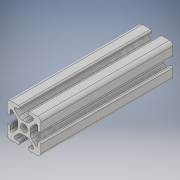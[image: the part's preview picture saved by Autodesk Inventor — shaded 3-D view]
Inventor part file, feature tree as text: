
AUTODESK INVENTOR PART (.ipt)
format: ipt  version: 2019.4 (Build 234330000, 330)  size: 232,448 bytes
history: native  units: mm
features: other x1, thicken_offset x1, extrude x1, sketch x1
ambient origin geometry x8: Origin, YZ Plane, XZ Plane, XY Plane, X Axis, Y Axis, Z Axis, Center Point
bodies: Solid1 (feature_tree)
feature tree (4):
  other  "Boss-Extrude1"
  thicken_offset  "Thicken1"
  extrude  "Extrusion3"  Depth=20.0mm
  sketch  "Sketch3"  dims[d5=45.19mm d6=45.19mm d7=20.0mm d8=20.0mm d9=273.0mm d10=0.0mm]
